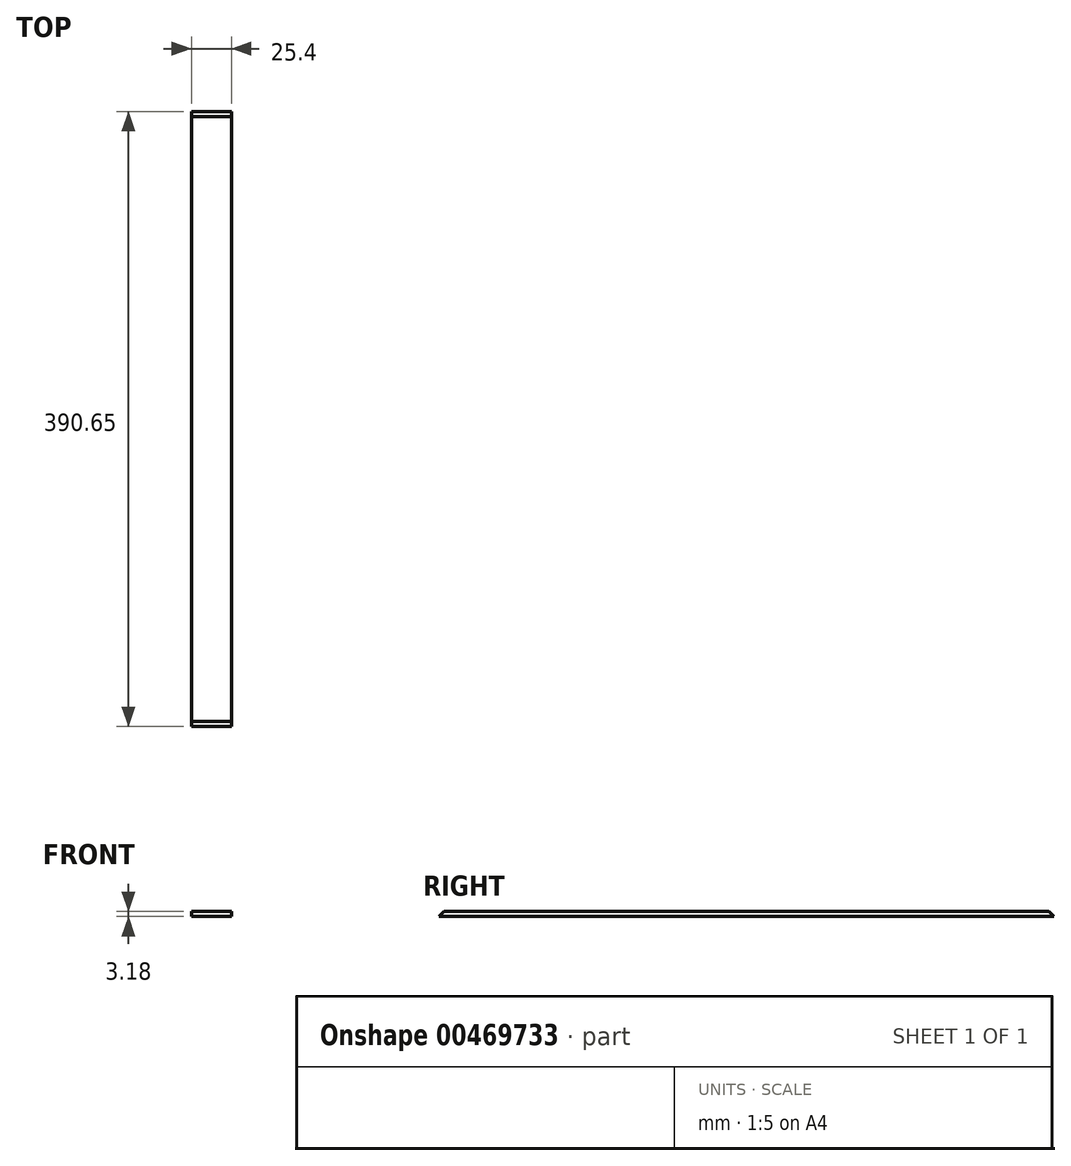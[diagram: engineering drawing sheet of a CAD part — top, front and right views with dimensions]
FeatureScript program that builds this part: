
annotation { "Feature Type Name" : "Feature", "Feature Type Description" : "" }
export const myFeature = defineFeature(function(context is Context, id is Id, definition is map)
    precondition{}
    {
        {
            var Q0;
            Q0=qCreatedBy(makeId("Right.planeOp"),FACE);
            var sketch = newSketch(context, id + "F0", { "sketchPlane" : qUnion([Q0])});
            skLineSegment(sketch, "E0.bottom", {"start": v(0, 0) * mm, "end": v(-390.65, 0) * mm});
            skLineSegment(sketch, "E0.top", {"start": v(0, 3.17) * mm, "end": v(-390.65, 3.17) * mm});
            skLineSegment(sketch, "E0.left", {"start": v(0, 0) * mm, "end": v(0, 3.17) * mm});
            skLineSegment(sketch, "E0.right", {"start": v(-390.65, 0) * mm, "end": v(-390.65, 3.17) * mm});
            skSolve(sketch);
        }
        {
            var Q0;
            Q0=makeQuery(id+"F0.imprint","IMPRINT",FACE,{"disambiguationData":[TD([[makeQuery(id+"F0.imprint","IMPRINT",EDGE,{"derivedFrom":sQuery(id+"F0.wireOp",EDGE,"E0.bottom")}),-1.0]])]});
            extrude(context, id + "F1", {"entities" : qUnion([Q0]), "depth" : 25.4 * mm, "offsetDistance" : 25.4 * mm});
        }
        {
            var Q0;
            Q0=makeQuery(id+"F1.opExtrude","SWEPT_EDGE",EDGE,{"disambiguationData":[OSD([sQuery(id+"F0.wireOp",EDGE,"E0.top"),sQuery(id+"F0.wireOp",EDGE,"E0.left")])]});
            chamfer(context, id + "F2", {"entities" : qUnion([Q0]), "width" : 3.17 * mm, "tangentPropagation" : true});
        }
        {
            var Q0;
            Q0=makeQuery(id+"F1.opExtrude","SWEPT_EDGE",EDGE,{"disambiguationData":[OSD([sQuery(id+"F0.wireOp",EDGE,"E0.top"),sQuery(id+"F0.wireOp",EDGE,"E0.right")])]});
            chamfer(context, id + "F3", {"entities" : qUnion([Q0]), "width" : 3.17 * mm, "tangentPropagation" : true});
        }
    });
